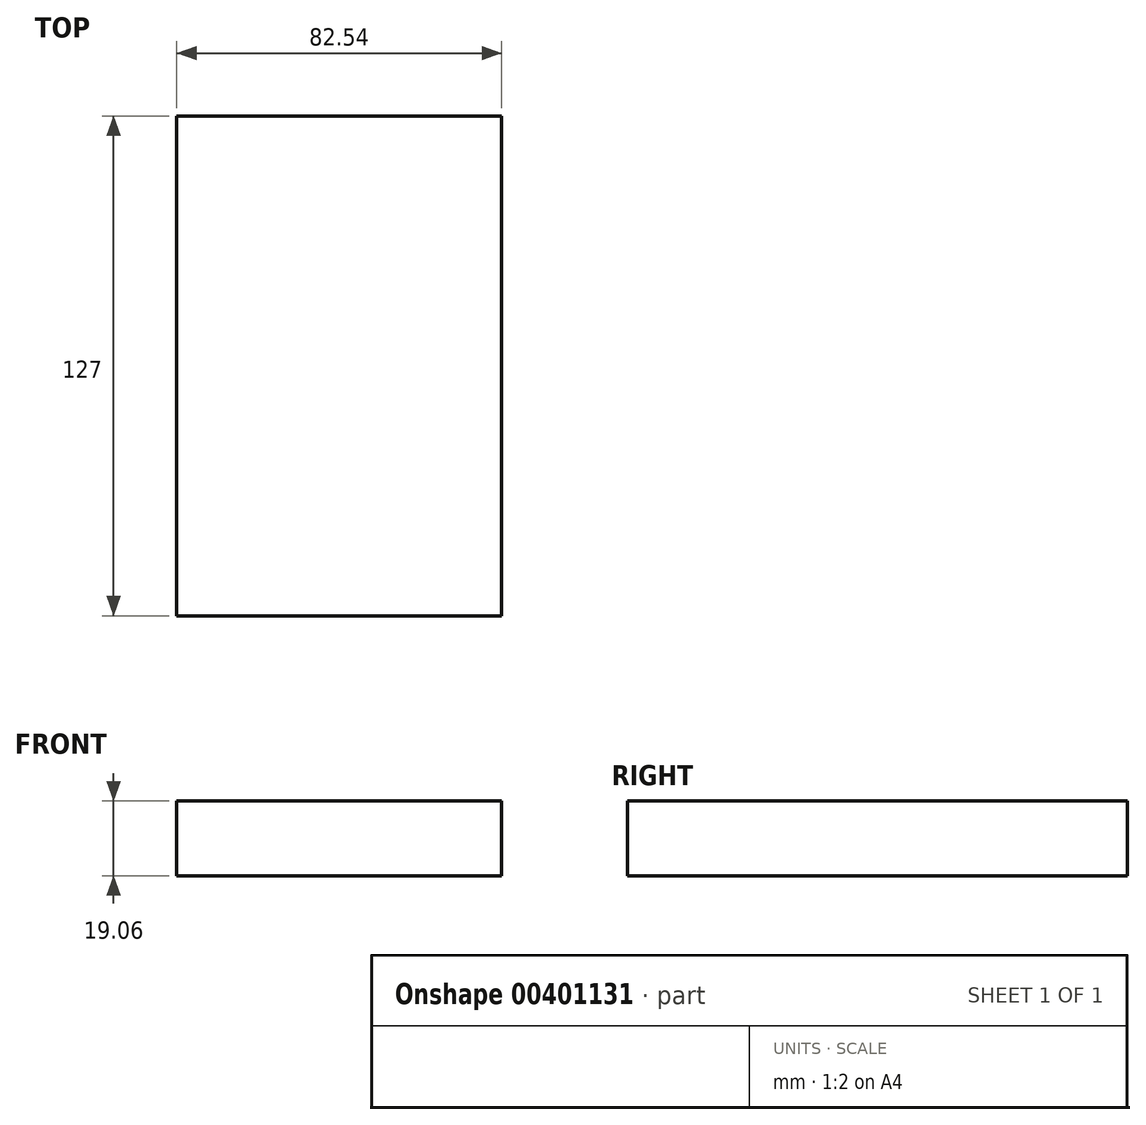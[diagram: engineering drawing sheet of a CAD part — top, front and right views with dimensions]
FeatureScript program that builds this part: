
annotation { "Feature Type Name" : "Feature", "Feature Type Description" : "" }
export const myFeature = defineFeature(function(context is Context, id is Id, definition is map)
    precondition{}
    {
        {
            var Q0;
            Q0=qCreatedBy(makeId("Front.planeOp"),FACE);
            var sketch = newSketch(context, id + "F0", { "sketchPlane" : qUnion([Q0])});
            skLineSegment(sketch, "E0.bottom", {"start": v(41.28, -9.52) * mm, "end": v(-41.28, -9.53) * mm});
            skLineSegment(sketch, "E0.top", {"start": v(41.27, 9.53) * mm, "end": v(-41.28, 9.52) * mm});
            skLineSegment(sketch, "E0.left", {"start": v(41.28, -9.52) * mm, "end": v(41.27, 9.53) * mm});
            skLineSegment(sketch, "E0.right", {"start": v(-41.27, -9.53) * mm, "end": v(-41.28, 9.52) * mm});
            skPoint(sketch, "E0.middle", {"position": v(0, 0) * mm});
            skLineSegment(sketch, "E1.bottom", {"start": v(87.81, 36.66) * mm, "end": v(164.01, 36.66) * mm});
            skLineSegment(sketch, "E1.top", {"start": v(87.81, 65.24) * mm, "end": v(164.01, 65.24) * mm});
            skLineSegment(sketch, "E1.left", {"start": v(87.81, 36.66) * mm, "end": v(87.81, 65.24) * mm});
            skLineSegment(sketch, "E1.right", {"start": v(164.01, 36.66) * mm, "end": v(164.01, 65.24) * mm});
            skPoint(sketch, "E1.middle", {"position": v(125.91, 50.95) * mm});
            skLineSegment(sketch, "E2", {"start": v(41.27, 9.53) * mm, "end": v(41.27, 34.93) * mm});
            skArc(sketch, "E3", {"start": v(41.28, 34.93) * mm, "mid": v(51.45, 59.5) * mm, "end": v(76.02, 69.67) * mm});
            skLineSegment(sketch, "E4", {"start": v(76.02, 69.67) * mm, "end": v(118.6, 69.67) * mm});
            skLineSegment(sketch, "E5", {"start": v(118.6, 69.67) * mm, "end": v(97.3, 69.67) * mm});
            skSolve(sketch);
        }
        {
            var Q0;
            Q0=makeQuery(id+"F0.imprint","IMPRINT",FACE,{"disambiguationData":[TD([[makeQuery(id+"F0.imprint","IMPRINT",EDGE,{"derivedFrom":sQuery(id+"F0.wireOp",EDGE,"E0.bottom")}),-1.0]])]});
            extrude(context, id + "F1", {"entities" : qUnion([Q0]), "endBound" : BoundingType.SYMMETRIC, "depth" : 127 * mm});
        }
    });
